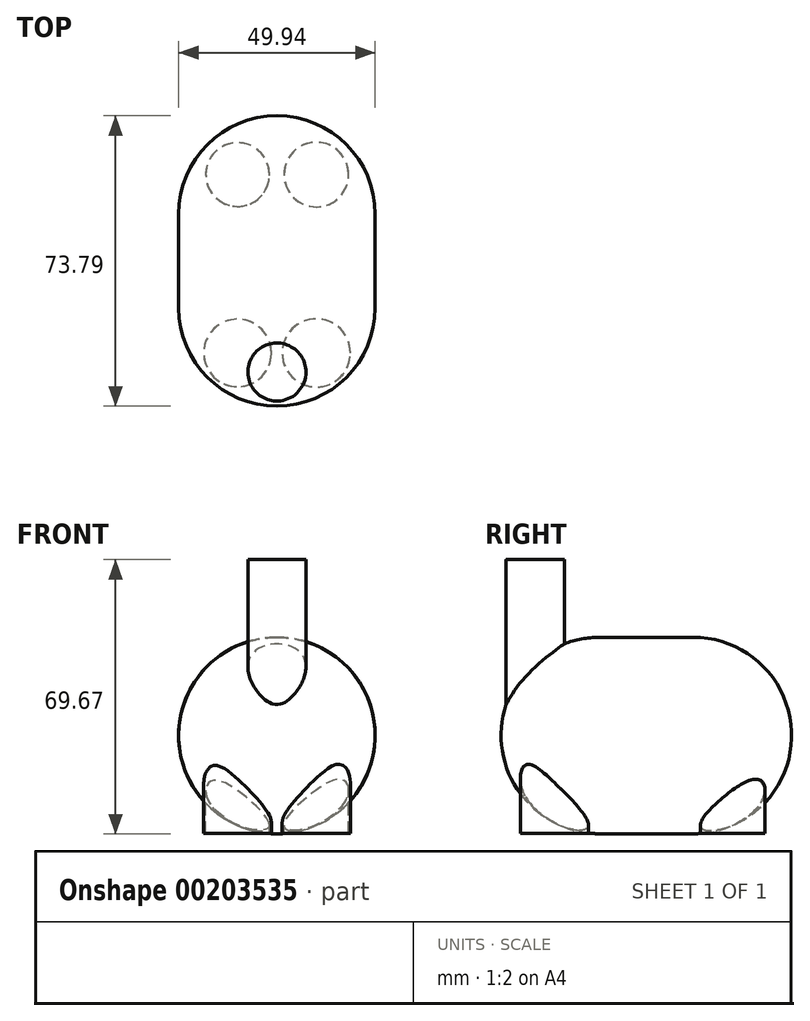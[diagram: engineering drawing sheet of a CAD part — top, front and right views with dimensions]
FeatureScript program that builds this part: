
annotation { "Feature Type Name" : "Feature", "Feature Type Description" : "" }
export const myFeature = defineFeature(function(context is Context, id is Id, definition is map)
    precondition{}
    {
        {
            var Q0;
            Q0=qCreatedBy(makeId("Front.planeOp"),FACE);
            var sketch = newSketch(context, id + "F0", { "sketchPlane" : qUnion([Q0])});
            skArc(sketch, "E0", {"start": v(0, -24.96) * mm, "mid": v(24.96, 0) * mm, "end": v(0, 24.96) * mm});
            skLineSegment(sketch, "E1", {"start": v(0, 0) * mm, "end": v(0, 24.96) * mm});
            skLineSegment(sketch, "E2", {"start": v(0, 24.96) * mm, "end": v(0, 0) * mm});
            skLineSegment(sketch, "E3", {"start": v(0, -24.96) * mm, "end": v(0, 0) * mm});
            skSolve(sketch);
        }
        {
            var Q0;
            Q0=makeQuery(id+"F0.imprint","IMPRINT",FACE,{"disambiguationData":[TD([[makeQuery(id+"F0.imprint","IMPRINT",EDGE,{"derivedFrom":sQuery(id+"F0.wireOp",EDGE,"E0")}),1.0]])]});
            var Q1;
            Q1=sQuery(id+"F0.wireOp",EDGE,"E2");
            revolve(context, id + "F1", {"entities" : qUnion([Q0]), "axis" : qUnion([Q1]), "revolveType" : RevolveType.ONE_DIRECTION, "angle" : 180 * degree});
        }
        {
            var Q0;
            Q0=qCreatedBy(makeId("Front.planeOp"),FACE);
            var sketch = newSketch(context, id + "F2", { "sketchPlane" : qUnion([Q0])});
            skCircle(sketch, "E4", {"center": v(0, 0) * mm, "radius": 24.97 * mm});
            skSolve(sketch);
        }
        {
            var Q0;
            Q0 = qSketchRegion(id + "F2", true);
            extrude(context, id + "F3", {"entities" : qUnion([Q0]), "operationType" : NewBodyOperationType.ADD, "oppositeDirection" : true, "depth" : 11.94 * mm});
        }
        {
            var Q0;
            Q0=makeQuery(id+"F1.opRevolve","SWEPT_BODY",BODY,{"disambiguationData":[OSD([sQuery(id+"F0.wireOp",EDGE,"E0"),sQuery(id+"F0.wireOp",EDGE,"E2"),sQuery(id+"F0.wireOp",EDGE,"E3")])]});
            var Q1;
            Q1=makeQuery(id+"F3.opExtrude","CAP_FACE",FACE,{"disambiguationData":[OSD([sQuery(id+"F2.wireOp",EDGE,"E4")])],"isStart":false});
            mirror(context, id + "F4", {"operationType" : NewBodyOperationType.ADD, "entities" : qUnion([Q0]), "mirrorPlane" : qUnion([Q1])});
        }
        {
            var Q0;
            Q0=qCreatedBy(makeId("Top.planeOp"),FACE);
            var sketch = newSketch(context, id + "F5", { "sketchPlane" : qUnion([Q0])});
            skCircle(sketch, "E5", {"center": v(10.01, -11.44) * mm, "radius": 8.67 * mm});
            skCircle(sketch, "E6", {"center": v(-10, -11.44) * mm, "radius": 8.59 * mm});
            skCircle(sketch, "E7", {"center": v(10.01, 33.87) * mm, "radius": 8.22 * mm});
            skCircle(sketch, "E8", {"center": v(-10, 33.87) * mm, "radius": 8.1 * mm});
            skSolve(sketch);
        }
        {
            var Q0;
            Q0 = qSketchRegion(id + "F5", true);
            extrude(context, id + "F6", {"entities" : qUnion([Q0]), "operationType" : NewBodyOperationType.ADD, "oppositeDirection" : true, "depth" : 24.87 * mm});
        }
        {
            var Q0;
            Q0=qCreatedBy(makeId("Top.planeOp"),FACE);
            var sketch = newSketch(context, id + "F7", { "sketchPlane" : qUnion([Q0])});
            skCircle(sketch, "E9", {"center": v(0, -16.3) * mm, "radius": 7.38 * mm});
            skSolve(sketch);
        }
        {
            var Q0;
            Q0 = qSketchRegion(id + "F7", true);
            extrude(context, id + "F8", {"entities" : qUnion([Q0]), "operationType" : NewBodyOperationType.ADD, "depth" : 44.7 * mm});
        }
        {
            var Q0;
            Q0=qCreatedBy(makeId("Top.planeOp"),FACE);
            cPlane(context, id + "F9", {"entities" : qUnion([Q0]), "cplaneType" : CPlaneType.OFFSET, "offset" : 50.8 * mm, "width" : 152.4 * mm, "height" : 152.4 * mm});
        }
    });
